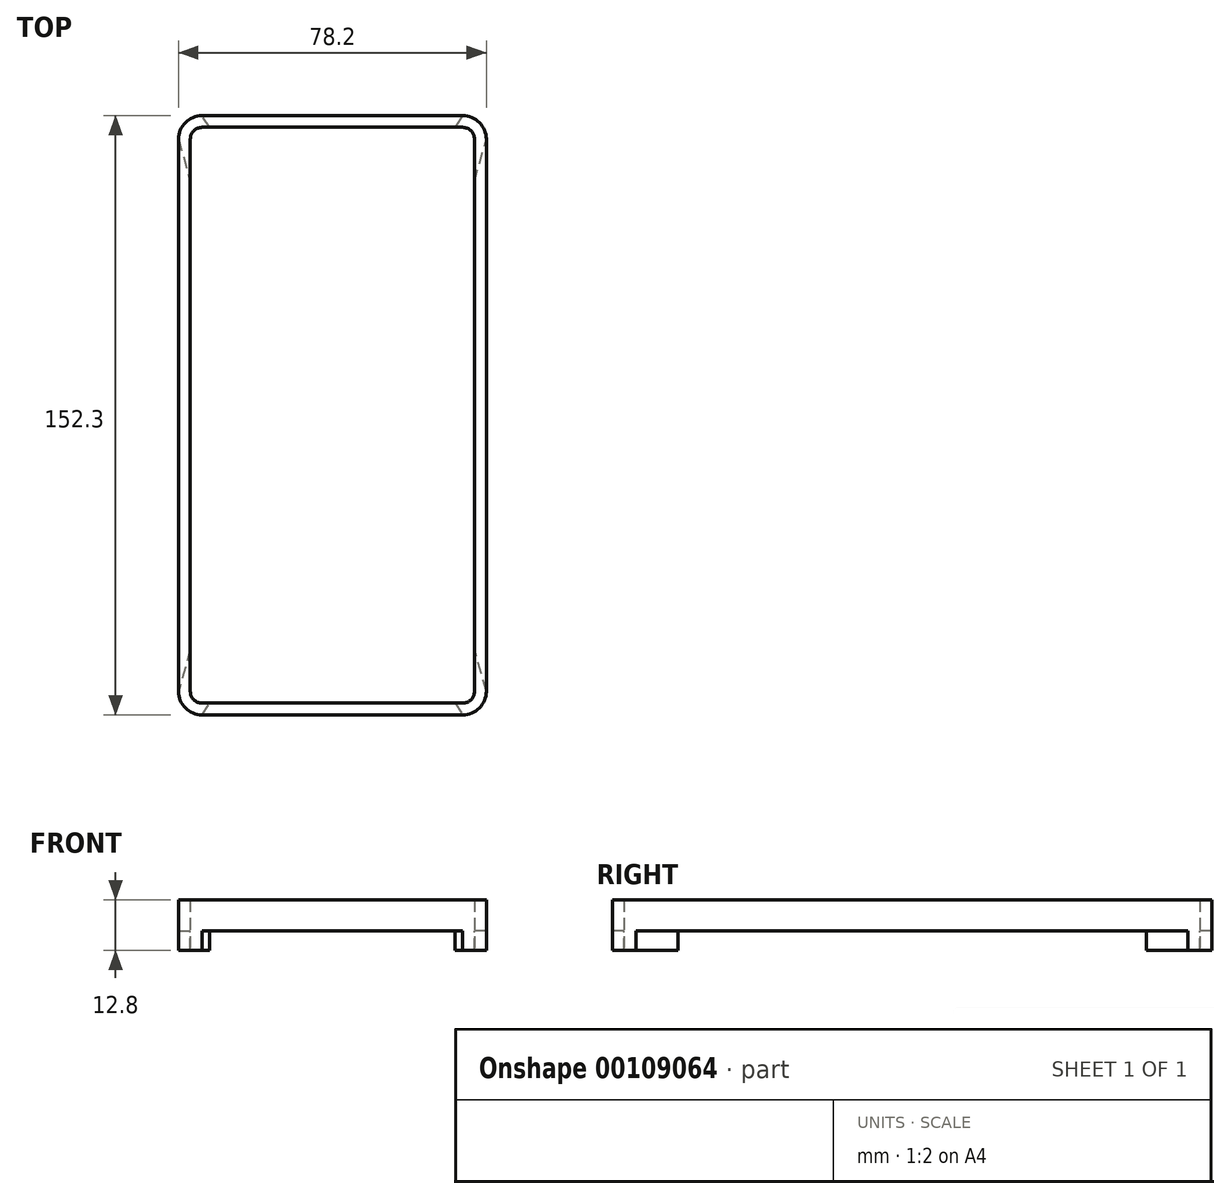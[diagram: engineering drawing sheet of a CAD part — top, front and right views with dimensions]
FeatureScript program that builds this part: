
annotation { "Feature Type Name" : "Feature", "Feature Type Description" : "" }
export const myFeature = defineFeature(function(context is Context, id is Id, definition is map)
    precondition{}
    {
        {
            var Q0;
            Q0=qCreatedBy(makeId("Top.planeOp"),FACE);
            var sketch = newSketch(context, id + "F0", { "sketchPlane" : qUnion([Q0])});
            skLineSegment(sketch, "E0.bottom", {"start": v(33.1, 73.15) * mm, "end": v(-33.1, 73.15) * mm});
            skLineSegment(sketch, "E0.top", {"start": v(33.1, -73.15) * mm, "end": v(-33.1, -73.15) * mm});
            skLineSegment(sketch, "E0.left", {"start": v(36.1, 70.15) * mm, "end": v(36.1, -70.15) * mm});
            skLineSegment(sketch, "E0.right", {"start": v(-36.1, 70.15) * mm, "end": v(-36.1, -70.15) * mm});
            skPoint(sketch, "E0.middle", {"position": v(0, 0) * mm});
            skPoint(sketch, "E1.visualSharp", {"position": v(-36.1, 73.15) * mm});
            skArc(sketch, "E1.filletArc", {"start": v(-33.1, 73.15) * mm, "mid": v(-35.22, 72.27) * mm, "end": v(-36.1, 70.15) * mm});
            skPoint(sketch, "E2.visualSharp", {"position": v(36.1, 73.15) * mm});
            skArc(sketch, "E2.filletArc", {"start": v(36.1, 70.15) * mm, "mid": v(35.22, 72.27) * mm, "end": v(33.1, 73.15) * mm});
            skPoint(sketch, "E3.visualSharp", {"position": v(-36.1, -73.15) * mm});
            skArc(sketch, "E3.filletArc", {"start": v(-36.1, -70.15) * mm, "mid": v(-35.22, -72.27) * mm, "end": v(-33.1, -73.15) * mm});
            skPoint(sketch, "E4.visualSharp", {"position": v(36.1, -73.15) * mm});
            skArc(sketch, "E4.filletArc", {"start": v(33.1, -73.15) * mm, "mid": v(35.22, -72.27) * mm, "end": v(36.1, -70.15) * mm});
            skArc(sketch, "E5.0", {"start": v(39.1, 70.15) * mm, "mid": v(37.34, 74.4) * mm, "end": v(33.1, 76.15) * mm});
            skLineSegment(sketch, "E5.1", {"start": v(39.1, 70.15) * mm, "end": v(39.1, -70.15) * mm});
            skLineSegment(sketch, "E5.2", {"start": v(33.1, 76.15) * mm, "end": v(-33.1, 76.15) * mm});
            skArc(sketch, "E5.3", {"start": v(33.1, -76.15) * mm, "mid": v(37.34, -74.4) * mm, "end": v(39.1, -70.15) * mm});
            skArc(sketch, "E5.4", {"start": v(-33.1, 76.15) * mm, "mid": v(-37.34, 74.4) * mm, "end": v(-39.1, 70.15) * mm});
            skLineSegment(sketch, "E5.5", {"start": v(-39.1, 70.15) * mm, "end": v(-39.1, -70.15) * mm});
            skArc(sketch, "E5.6", {"start": v(-39.1, -70.15) * mm, "mid": v(-37.34, -74.4) * mm, "end": v(-33.1, -76.15) * mm});
            skLineSegment(sketch, "E5.7", {"start": v(33.1, -76.15) * mm, "end": v(-33.1, -76.15) * mm});
            skSolve(sketch);
        }
        {
            var Q0;
            Q0=makeQuery(id+"F0.imprint","IMPRINT",FACE,{"disambiguationData":[TD([[makeQuery(id+"F0.imprint","IMPRINT",EDGE,{"derivedFrom":sQuery(id+"F0.wireOp",EDGE,"E0.bottom")}),-1.0]])]});
            extrude(context, id + "F1", {"entities" : qUnion([Q0]), "depth" : 7.8 * mm});
        }
        {
            var Q0;
            Q0=makeQuery(id+"F1.opExtrude","CAP_FACE",FACE,{"disambiguationData":[OSD([sQuery(id+"F0.wireOp",EDGE,"E0.bottom"),sQuery(id+"F0.wireOp",EDGE,"E0.top"),sQuery(id+"F0.wireOp",EDGE,"E0.left"),sQuery(id+"F0.wireOp",EDGE,"E0.right"),sQuery(id+"F0.wireOp",EDGE,"E1.filletArc"),sQuery(id+"F0.wireOp",EDGE,"E2.filletArc"),sQuery(id+"F0.wireOp",EDGE,"E3.filletArc"),sQuery(id+"F0.wireOp",EDGE,"E4.filletArc"),sQuery(id+"F0.wireOp",EDGE,"E5.0"),sQuery(id+"F0.wireOp",EDGE,"E5.1"),sQuery(id+"F0.wireOp",EDGE,"E5.2"),sQuery(id+"F0.wireOp",EDGE,"E5.3"),sQuery(id+"F0.wireOp",EDGE,"E5.4"),sQuery(id+"F0.wireOp",EDGE,"E5.5"),sQuery(id+"F0.wireOp",EDGE,"E5.6"),sQuery(id+"F0.wireOp",EDGE,"E5.7")])],"isStart":true});
            var sketch = newSketch(context, id + "F2", { "sketchPlane" : qUnion([Q0])});
            skArc(sketch, "E6.0.1", {"start": v(-33.1, 76.15) * mm, "mid": v(-37.34, 74.4) * mm, "end": v(-39.1, 70.15) * mm});
            skArc(sketch, "E6.0.3", {"start": v(-39.1, -70.15) * mm, "mid": v(-37.34, -74.4) * mm, "end": v(-33.1, -76.15) * mm});
            skArc(sketch, "E6.0.5", {"start": v(33.1, -76.15) * mm, "mid": v(37.34, -74.4) * mm, "end": v(39.1, -70.15) * mm});
            skArc(sketch, "E6.0.7", {"start": v(39.1, 70.15) * mm, "mid": v(37.34, 74.4) * mm, "end": v(33.1, 76.15) * mm});
            skPoint(sketch, "E7.middle", {"position": v(0, 0) * mm});
            skLineSegment(sketch, "E8", {"start": v(-33.1, 76.15) * mm, "end": v(-4.2, 31.27) * mm});
            skLineSegment(sketch, "E9", {"start": v(4.2, 31.27) * mm, "end": v(33.1, 76.15) * mm});
            skLineSegment(sketch, "E10", {"start": v(39.1, 70.15) * mm, "end": v(19.7, 1.36) * mm});
            skLineSegment(sketch, "E11", {"start": v(19.7, -1.36) * mm, "end": v(39.1, -70.15) * mm});
            skLineSegment(sketch, "E12", {"start": v(33.1, -76.15) * mm, "end": v(4.2, -31.27) * mm});
            skLineSegment(sketch, "E13", {"start": v(-4.2, -31.27) * mm, "end": v(-33.1, -76.15) * mm});
            skLineSegment(sketch, "E14", {"start": v(-39.1, -70.15) * mm, "end": v(-19.7, -1.36) * mm});
            skLineSegment(sketch, "E15", {"start": v(-19.7, 1.36) * mm, "end": v(-39.1, 70.15) * mm});
            skPoint(sketch, "E16.orphan", {"position": v(-19.32, 24.74) * mm});
            skPoint(sketch, "E17.orphan", {"position": v(19.32, 24.74) * mm});
            skPoint(sketch, "E18.orphan", {"position": v(19.32, -24.74) * mm});
            skPoint(sketch, "E7.right.end.orphan", {"position": v(-19.32, -24.74) * mm});
            skPoint(sketch, "E19.visualSharp", {"position": v(0, 24.74) * mm});
            skArc(sketch, "E19.filletArc", {"start": v(-4.2, 31.27) * mm, "mid": v(0, 28.98) * mm, "end": v(4.2, 31.27) * mm});
            skPoint(sketch, "E20.visualSharp", {"position": v(0, -24.74) * mm});
            skArc(sketch, "E20.filletArc", {"start": v(4.2, -31.27) * mm, "mid": v(0, -28.98) * mm, "end": v(-4.2, -31.27) * mm});
            skPoint(sketch, "E21.visualSharp", {"position": v(19.32, 0) * mm});
            skArc(sketch, "E21.filletArc", {"start": v(19.7, 1.36) * mm, "mid": v(19.52, 0) * mm, "end": v(19.7, -1.36) * mm});
            skPoint(sketch, "E22.visualSharp", {"position": v(-19.32, 0) * mm});
            skArc(sketch, "E22.filletArc", {"start": v(-19.7, -1.36) * mm, "mid": v(-19.52, 0) * mm, "end": v(-19.7, 1.36) * mm});
            skSolve(sketch);
        }
        {
            var Q0;
            {var subQ17=sQuery(id+"F2.wireOp",EDGE,"E19.filletArc");Q0=makeQuery(id+"F2.imprint","IMPRINT",FACE,{"disambiguationData":[TD([[makeQuery(id+"F2.imprint","IMPRINT",EDGE,{"derivedFrom":subQ17}),-1.0]])]});}
            var Q1;
            {var subQ2=sQuery(id+"F2.wireOp",EDGE,"E6.0.1");Q1=makeQuery(id+"F2.imprint","IMPRINT",FACE,{"disambiguationData":[TD([[makeQuery(id+"F2.imprint","IMPRINT",EDGE,{"derivedFrom":subQ2}),-1.0]])]});}
            var Q2;
            {var subQ2=sQuery(id+"F2.wireOp",EDGE,"E6.0.7");Q2=makeQuery(id+"F2.imprint","IMPRINT",FACE,{"disambiguationData":[TD([[makeQuery(id+"F2.imprint","IMPRINT",EDGE,{"derivedFrom":subQ2}),-1.0]])]});}
            var Q3;
            {var subQ2=sQuery(id+"F2.wireOp",EDGE,"E6.0.5");Q3=makeQuery(id+"F2.imprint","IMPRINT",FACE,{"disambiguationData":[TD([[makeQuery(id+"F2.imprint","IMPRINT",EDGE,{"derivedFrom":subQ2}),-1.0]])]});}
            var Q4;
            {var subQ2=sQuery(id+"F2.wireOp",EDGE,"E6.0.3");Q4=makeQuery(id+"F2.imprint","IMPRINT",FACE,{"disambiguationData":[TD([[makeQuery(id+"F2.imprint","IMPRINT",EDGE,{"derivedFrom":subQ2}),-1.0]])]});}
            extrude(context, id + "F3", {"entities" : qUnion([Q0, Q1, Q2, Q3, Q4]), "operationType" : NewBodyOperationType.ADD, "depth" : 5 * mm});
        }
    });
